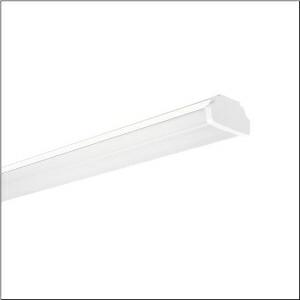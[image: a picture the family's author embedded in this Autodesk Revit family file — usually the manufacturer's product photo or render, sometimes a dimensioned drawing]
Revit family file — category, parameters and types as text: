
# Revit family: modario_31_gen_2_53bm8127v485c2_b318
name_source: partatom
category: Lighting Fixtures
units: mm (PartAtom-declared; Revit-internal decimal feet)

## family parameters
Cut with Voids When Loaded = No
Host = Face
Light Source = No
Part Type = Normal
Room Calculation Point = No
Round Connector Dimension = Use Diameter
Shared = No

## types (1)
- Modario 31 Gen.2 (1 x LED, 8590 lm, 47.9 W, 4000K)
    Apparent Load = 48 VA
    CIE Flux Codes = 47 80 95 93 100
    Color Rendering = 80
    Color Temperature = 4000K
    Default Elevation = 1800 mm
    Description = Modario 31 Gen.2, luminaire insert, of sheet steel, coil coated, white, length: 1.495mm, width: 81mm, height: 82mm, 5x system unit, system units: 299mm, LED rated luminous flux: 8.590lm, light colour: 840, SDCM (Standard Deviation of Colour Matching)MacAdam ≤ 3 SDCM (initial), control gear: ON/OFF, control gear: ECG, with plug, 3-pole, with phase selection, mains connection: 220..240V, AC, 50/60Hz, rated input power: 48W, through-wiring accessed according to module size, primary optical cover: cover, of PMMA, light emission: direct distribution, primary light characteristic: symmetric, protection rating (complete): IP20, protection rating (LED compartment): IP50, insulation class (complete): insulation class I (protective earthing), certification: CE, ENEC, VDE, UKCA, impact resistance: IK03, permissible ambient temperature for indoor applications: -35..+45°C, corresponds to IFS (International Featured Standards) requirements for safety and quality in the food industry, reducing of maximum allowable ambient temperature of 5°C with ceiling mounting, IP40 when using the optional accessory 5TP9018, packaging unit: 1 piece
    Height = 92 mm
    Lamp = 1 x LED
    Lamp Light Flux = 8590 lm
    Lamp Power = 47.9 W
    Lamp count = 1
    Length = 1495 mm
    Luminous efficacy = 179 lm/W
    Manufacturer = Siteco
    ModVariant = No
    Model = 53BM8127V485C2
    Mounting Place = Ceiling
    Mounting Type = Pendant
    Number of Poles = 1
    OnlyDefault = Yes
    Power Factor = 1
    Product Name = Modario 31 Gen.2
    Product group = luminaire insert | ceiling pendant
    ProductGroupID = 901
    Protection Class = Protection class I
    Protection Degree = IP 20
    RLX_Detail_Level = 1
    RLX_Emergency_Light_Flux = 0 lm
    RLX_Emergency_Type = 0
    RLX_Emergency_Type_DB = No
    RlxData = <blob elided: 38689 chars, md5=c7dc520b>
    Socket = socket
    Standby Power = 0 W
    System Light Flux = 8590 lm
    System Power = 48 W
    Type Comments = Product without accessories
    Type Image = l_1341886.jpg
    URL = http://relux.com
    VarID = ---
    Voltage = 0 V
    Weight = 0.00 kg
    Width = 81 mm

## geometry (parser evidence)
native form markers: Blend x4, Sweep x14
no freeform markers — native parametric forms only
